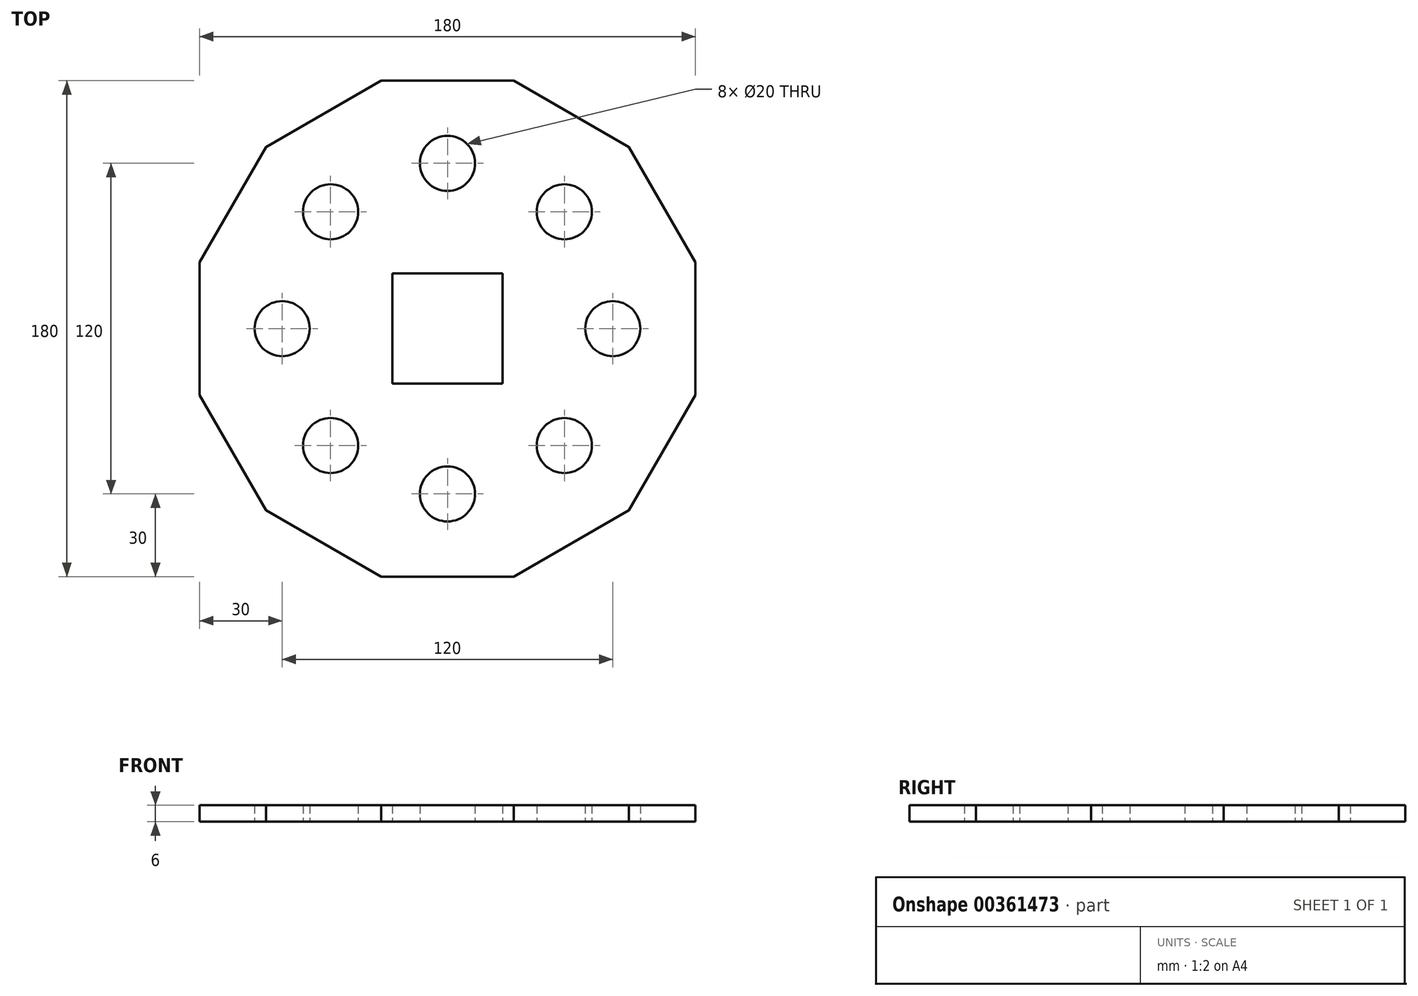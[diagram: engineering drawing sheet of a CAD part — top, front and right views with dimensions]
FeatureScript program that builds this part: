
annotation { "Feature Type Name" : "Feature", "Feature Type Description" : "" }
export const myFeature = defineFeature(function(context is Context, id is Id, definition is map)
    precondition{}
    {
        {
            var Q0;
            Q0=qCreatedBy(makeId("Top.planeOp"),FACE);
            var sketch = newSketch(context, id + "F0", { "sketchPlane" : qUnion([Q0])});
            skCircle(sketch, "E0.cCircle", {"center": v(0, 0) * mm, "radius": 93.17 * mm, "construction": true});
            skLineSegment(sketch, "E0.0", {"start": v(65.88, -65.88) * mm, "end": v(24.12, -90) * mm});
            skLineSegment(sketch, "E0.1", {"start": v(24.12, -90) * mm, "end": v(-24.12, -90) * mm});
            skLineSegment(sketch, "E0.2", {"start": v(-24.12, -90) * mm, "end": v(-65.88, -65.88) * mm});
            skLineSegment(sketch, "E0.3", {"start": v(-65.88, -65.88) * mm, "end": v(-90, -24.12) * mm});
            skLineSegment(sketch, "E0.4", {"start": v(-90, -24.12) * mm, "end": v(-90, 24.12) * mm});
            skLineSegment(sketch, "E0.5", {"start": v(-90, 24.12) * mm, "end": v(-65.88, 65.88) * mm});
            skLineSegment(sketch, "E0.6", {"start": v(-65.88, 65.88) * mm, "end": v(-24.12, 90) * mm});
            skLineSegment(sketch, "E0.8", {"start": v(24.12, 90) * mm, "end": v(65.88, 65.88) * mm});
            skLineSegment(sketch, "E0.9", {"start": v(65.88, 65.88) * mm, "end": v(90, 24.12) * mm});
            skLineSegment(sketch, "E0.10", {"start": v(90, 24.12) * mm, "end": v(90, -24.12) * mm});
            skLineSegment(sketch, "E0.11", {"start": v(90, -24.12) * mm, "end": v(65.88, -65.88) * mm});
            skCircle(sketch, "E1", {"center": v(0, 0) * mm, "radius": 60 * mm});
            skLineSegment(sketch, "E2", {"start": v(-24.12, 90) * mm, "end": v(24.12, 90) * mm});
            skLineSegment(sketch, "E3.bottom", {"start": v(-20, 20) * mm, "end": v(20, 20) * mm});
            skLineSegment(sketch, "E3.top", {"start": v(-20, -20) * mm, "end": v(20, -20) * mm});
            skLineSegment(sketch, "E3.left", {"start": v(-20, 20) * mm, "end": v(-20, -20) * mm});
            skLineSegment(sketch, "E3.right", {"start": v(20, 20) * mm, "end": v(20, -20) * mm});
            skCircle(sketch, "E4", {"center": v(0, 60) * mm, "radius": 10 * mm});
            skCircle(sketch, "E5", {"center": v(60, 0) * mm, "radius": 10 * mm});
            skCircle(sketch, "E6", {"center": v(0, -60) * mm, "radius": 10 * mm});
            skCircle(sketch, "E7", {"center": v(-60, 0) * mm, "radius": 10 * mm});
            skCircle(sketch, "E8", {"center": v(-42.43, 42.43) * mm, "radius": 10 * mm});
            skCircle(sketch, "E9", {"center": v(42.43, 42.43) * mm, "radius": 10 * mm});
            skCircle(sketch, "E10", {"center": v(42.43, -42.43) * mm, "radius": 10 * mm});
            skCircle(sketch, "E11", {"center": v(-42.43, -42.43) * mm, "radius": 10 * mm});
            skLineSegment(sketch, "E12", {"start": v(-42.43, 42.43) * mm, "end": v(0, 0) * mm});
            skLineSegment(sketch, "E13", {"start": v(42.43, 42.43) * mm, "end": v(0, 0) * mm});
            skLineSegment(sketch, "E14", {"start": v(0, 0) * mm, "end": v(42.43, -42.43) * mm});
            skLineSegment(sketch, "E15", {"start": v(0, 0) * mm, "end": v(-42.43, -42.43) * mm});
            skSolve(sketch);
        }
        {
            var Q0;
            Q0=makeQuery(id+"F0.imprint","IMPRINT",FACE,{"disambiguationData":[TD([[makeQuery(id+"F0.imprint","IMPRINT",EDGE,{"derivedFrom":sQuery(id+"F0.wireOp",EDGE,"E0.0")}),-1.0]])]});
            var Q1;
            {var subQ6=sQuery(id+"F0.wireOp",EDGE,"E3.left");Q1=makeQuery(id+"F0.imprint","IMPRINT",FACE,{"disambiguationData":[TD([[makeQuery(id+"F0.imprint","IMPRINT",EDGE,{"derivedFrom":subQ6}),-1.0]])]});}
            var Q2;
            {var subQ0=sQuery(id+"F0.wireOp",EDGE,"E3.bottom");Q2=makeQuery(id+"F0.imprint","IMPRINT",FACE,{"disambiguationData":[TD([[makeQuery(id+"F0.imprint","IMPRINT",EDGE,{"derivedFrom":subQ0}),1.0]])]});}
            var Q3;
            {var subQ5=sQuery(id+"F0.wireOp",EDGE,"E3.right");Q3=makeQuery(id+"F0.imprint","IMPRINT",FACE,{"disambiguationData":[TD([[makeQuery(id+"F0.imprint","IMPRINT",EDGE,{"derivedFrom":subQ5}),1.0]])]});}
            var Q4;
            {var subQ8=sQuery(id+"F0.wireOp",EDGE,"E3.top");Q4=makeQuery(id+"F0.imprint","IMPRINT",FACE,{"disambiguationData":[TD([[makeQuery(id+"F0.imprint","IMPRINT",EDGE,{"derivedFrom":subQ8}),-1.0]])]});}
            extrude(context, id + "F1", {"entities" : qUnion([Q0, Q1, Q2, Q3, Q4]), "depth" : 6 * mm});
        }
    });
